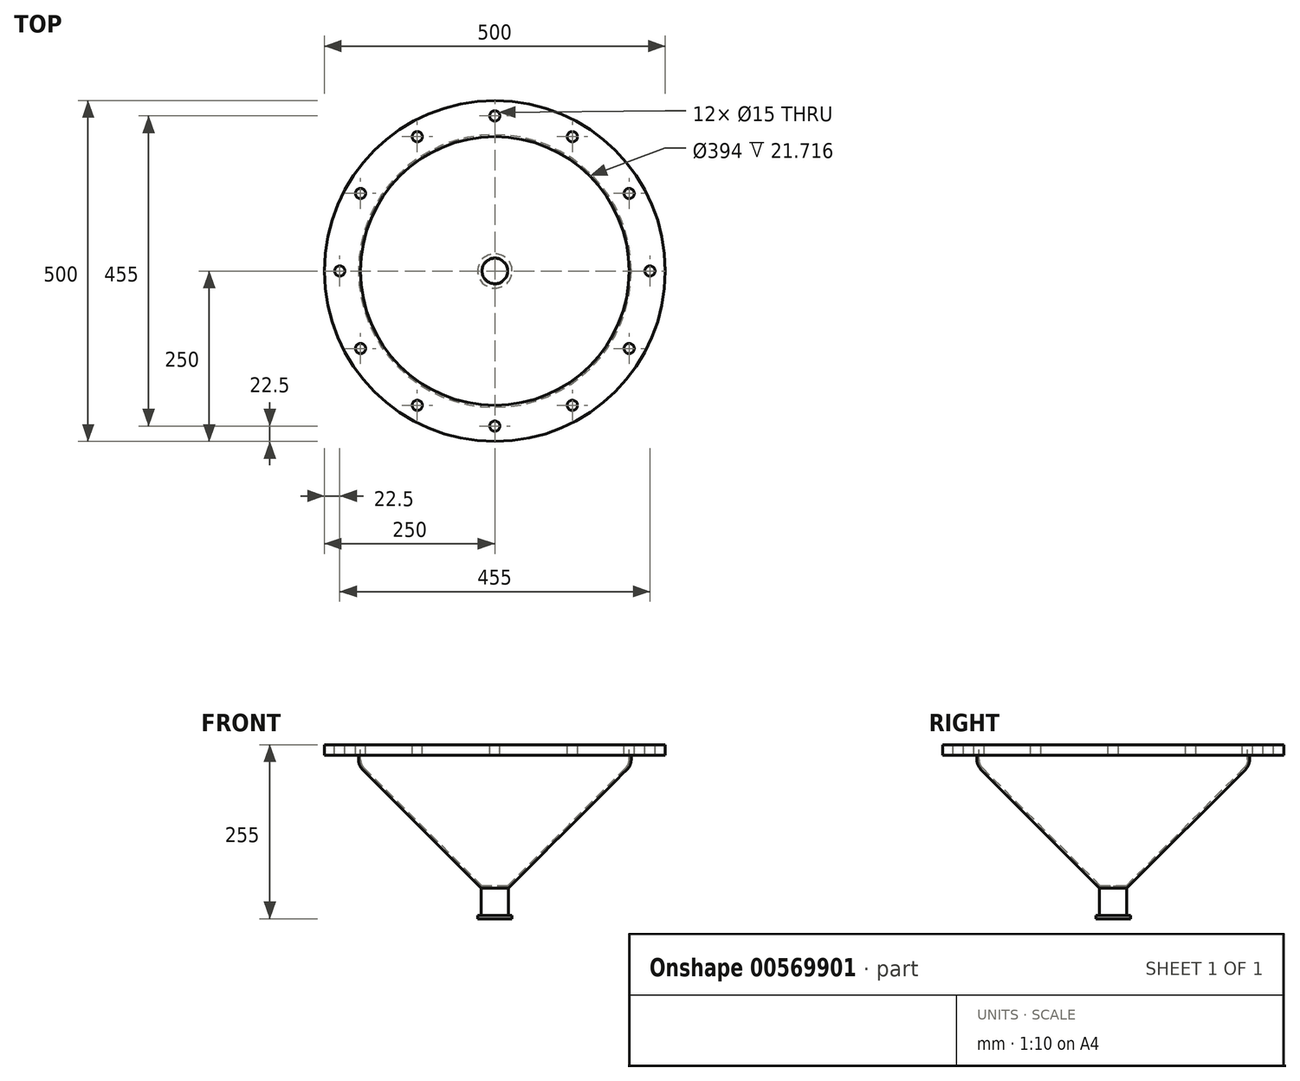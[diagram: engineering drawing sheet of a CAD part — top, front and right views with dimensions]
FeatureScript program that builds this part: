
annotation { "Feature Type Name" : "Feature", "Feature Type Description" : "" }
export const myFeature = defineFeature(function(context is Context, id is Id, definition is map)
    precondition{}
    {
        {
            var Q0;
            Q0=qCreatedBy(makeId("Top.planeOp"),FACE);
            var sketch = newSketch(context, id + "F0", { "sketchPlane" : qUnion([Q0])});
            skCircle(sketch, "E0", {"center": v(0, 0) * mm, "radius": 250 * mm});
            skCircle(sketch, "E1", {"center": v(0, 0) * mm, "radius": 200 * mm});
            skSolve(sketch);
        }
        {
            var Q0;
            Q0=qSketchRegion(id+"F0",true);
            extrude(context, id + "F1", {"entities" : qUnion([Q0]), "depth" : 15 * mm, "offsetDistance" : 25 * mm});
        }
        {
            var Q0;
            Q0=qCreatedBy(makeId("Front.planeOp"),FACE);
            var sketch = newSketch(context, id + "F2", { "sketchPlane" : qUnion([Q0])});
            skLineSegment(sketch, "E2", {"start": v(200, 15) * mm, "end": v(200, -6.72) * mm});
            skLineSegment(sketch, "E3", {"start": v(194.14, -20.86) * mm, "end": v(20, -195) * mm});
            skLineSegment(sketch, "E4", {"start": v(20, -195) * mm, "end": v(0, -195) * mm});
            skPoint(sketch, "E5.visualSharp", {"position": v(200, -15) * mm});
            skArc(sketch, "E5.filletArc", {"start": v(194.14, -20.86) * mm, "mid": v(198.48, -14.37) * mm, "end": v(200, -6.72) * mm});
            skLineSegment(sketch, "E6.0", {"start": v(18.76, -192) * mm, "end": v(0, -192) * mm});
            skLineSegment(sketch, "E6.1", {"start": v(192.02, -18.74) * mm, "end": v(18.76, -192) * mm});
            skArc(sketch, "E6.2", {"start": v(192.02, -18.74) * mm, "mid": v(195.7, -13.22) * mm, "end": v(197, -6.72) * mm});
            skLineSegment(sketch, "E6.3", {"start": v(197, 15) * mm, "end": v(197, -6.72) * mm});
            skLineSegment(sketch, "E7", {"start": v(197, 15) * mm, "end": v(200, 15) * mm});
            skLineSegment(sketch, "E8", {"start": v(0, -192) * mm, "end": v(0, -195) * mm});
            skSolve(sketch);
        }
        {
            var Q0;
            Q0=qSketchRegion(id+"F2",true);
            var Q1;
            Q1=sQuery(id+"F2.wireOp",EDGE,"E8");
            revolve(context, id + "F3", {"operationType" : NewBodyOperationType.ADD, "entities" : qUnion([Q0]), "axis" : qUnion([Q1]), "revolveType" : RevolveType.FULL});
        }
        {
            var Q0;
            Q0=makeQuery(id+"F3.boolean.opBoolean","MERGE",FACE,{"derivedFrom":[makeQuery(id+"F1.opExtrude","CAP_FACE",FACE,{"disambiguationData":[OSD([sQuery(id+"F0.wireOp",EDGE,"E0"),sQuery(id+"F0.wireOp",EDGE,"E1")])],"isStart":false}),makeQuery(id+"F3.opRevolve","SWEPT_FACE",FACE,{"disambiguationData":[OSD([sQuery(id+"F2.wireOp",EDGE,"E7")])]})]});
            var sketch = newSketch(context, id + "F4", { "sketchPlane" : qUnion([Q0])});
            skCircle(sketch, "E9", {"center": v(227.5, 0) * mm, "radius": 7.5 * mm});
            skCircle(sketch, "E10.1.0", {"center": v(197.02, 113.75) * mm, "radius": 7.5 * mm});
            skCircle(sketch, "E10.2.0", {"center": v(113.75, 197.02) * mm, "radius": 7.5 * mm});
            skCircle(sketch, "E10.3.0", {"center": v(0, 227.5) * mm, "radius": 7.5 * mm});
            skCircle(sketch, "E10.4.0", {"center": v(-113.75, 197.02) * mm, "radius": 7.5 * mm});
            skCircle(sketch, "E10.5.0", {"center": v(-197.02, 113.75) * mm, "radius": 7.5 * mm});
            skCircle(sketch, "E10.6.0", {"center": v(-227.5, 0) * mm, "radius": 7.5 * mm});
            skCircle(sketch, "E10.7.0", {"center": v(-197.02, -113.75) * mm, "radius": 7.5 * mm});
            skCircle(sketch, "E10.8.0", {"center": v(-113.75, -197.02) * mm, "radius": 7.5 * mm});
            skCircle(sketch, "E10.9.0", {"center": v(0, -227.5) * mm, "radius": 7.5 * mm});
            skCircle(sketch, "E10.10.0", {"center": v(113.75, -197.02) * mm, "radius": 7.5 * mm});
            skCircle(sketch, "E10.11.0", {"center": v(197.02, -113.75) * mm, "radius": 7.5 * mm});
            skPoint(sketch, "E10.center", {"position": v(0, 0) * mm});
            skSolve(sketch);
        }
        {
            var Q0;
            Q0=qSketchRegion(id+"F4",true);
            extrude(context, id + "F5", {"entities" : qUnion([Q0]), "operationType" : NewBodyOperationType.REMOVE, "endBound" : BoundingType.UP_TO_NEXT, "oppositeDirection" : true, "depth" : 25 * mm, "offsetDistance" : 25 * mm});
        }
        {
            var Q0;
            Q0=makeQuery(id+"F3.opRevolve","SWEPT_FACE",FACE,{"disambiguationData":[OSD([sQuery(id+"F2.wireOp",EDGE,"E4")])]});
            var sketch = newSketch(context, id + "F6", { "sketchPlane" : qUnion([Q0])});
            skCircle(sketch, "E11", {"center": v(0, 0) * mm, "radius": 20 * mm});
            skSolve(sketch);
        }
        {
            var Q0;
            Q0 = qSketchRegion(id + "F6", true);
            extrude(context, id + "F7", {"entities" : qUnion([Q0]), "operationType" : NewBodyOperationType.ADD, "depth" : 40 * mm, "offsetDistance" : 25 * mm});
        }
        {
            var Q0;
            Q0=makeQuery(id+"F7.opExtrude","CAP_FACE",FACE,{"disambiguationData":[OSD([sQuery(id+"F6.wireOp",EDGE,"E11")])],"isStart":false});
            var sketch = newSketch(context, id + "F8", { "sketchPlane" : qUnion([Q0])});
            skCircle(sketch, "E12", {"center": v(0, 0) * mm, "radius": 25.25 * mm});
            skSolve(sketch);
        }
        {
            var Q0;
            Q0 = qSketchRegion(id + "F8", true);
            extrude(context, id + "F9", {"entities" : qUnion([Q0]), "operationType" : NewBodyOperationType.ADD, "depth" : 5 * mm, "offsetDistance" : 25 * mm});
        }
    });
